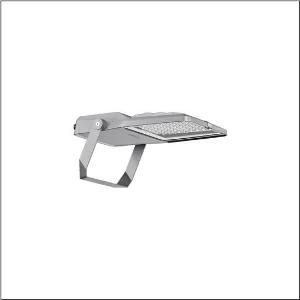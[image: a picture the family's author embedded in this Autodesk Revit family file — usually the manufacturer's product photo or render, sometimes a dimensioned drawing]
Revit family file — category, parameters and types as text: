
# Revit family: floodlight_fl_21_iq_mini___rs12_5xa7772b1b1a_07b1
name_source: partatom
category: Lighting Fixtures
units: mm (PartAtom-declared; Revit-internal decimal feet)

## family parameters
Cut with Voids When Loaded = No
Host = Face
Light Source = No
Part Type = Normal
Room Calculation Point = No
Round Connector Dimension = Use Diameter
Shared = No

## types (1)
- --- (1 x LED, 5230 lm, 45.5 W, 2200K)
    Apparent Load = 46 VA
    CIE Flux Codes = 79 92 99 100 100
    Color Rendering = 70
    Color Temperature = 2200K
    Default Elevation = 1800 mm
    Description = Floodlight FL 21 iQ mini, floodlight, primary light control with lens, of PMMA, primary optical cover: protective disc, of toughened safety glass, transparent, light distribution: RS12, light emission: direct distribution, installation type: surface-mounted, LED, High Power LED, rated luminous flux: 5.230lm, luminous efficacy: 115lm/W, light colour: 722, colour temperature: 2200K, control: Street-Remote, Auto-Match, Temp-Guard, Night-Set, Smart-Wire, Desk-Remote (wireless, voltage-free reading and setting of iQ features in the workshop via application-optimized NFC function/RFID function), optimised constant luminous flux control (CLO 2.0), with terminal, 6-pole, mains connection: 220..240V, AC, 50/60Hz, start of lifetime: 46W, end of service life: 48W, reduction: 21W, luminaire housing, of diecast aluminium, powder-coated, Siteco® metallic grey (DB 702S), corrosivity category C5 mid according to DIN EN ISO 12944, sealing non-destructively replaceable, mounting bracket, of steel, galvanised, powder-coated, Siteco® metallic grey (DB 702S), protection rating (complete): IP66, insulation class (complete): insulation class II (safety insulation), certification: CE, ENEC, VDE, protection symbol: D, impact resistance: IK08, permissible operating ambient temperature: -40..+40°C, permissible operating ambient temperature for outdoor applications: -40..+50°C, standard: DIN EN 12944, LABS conformity tested according to VDMA 24364:2018-05, packaging unit: 1 piece

Light Distribution: RS12
    Height = 70 mm
    Lamp = 1 x LED
    Lamp Light Flux = 5230 lm
    Lamp Power = 45.5 W
    Lamp count = 1
    Length = 485 mm
    Luminous efficacy = 115 lm/W
    Manufacturer = Siteco
    ModVariant = No
    Model = 5XA7772B1B1A
    Number of Poles = 1
    OnlyDefault = Yes
    Power Factor = 1
    Product Name = Floodlight FL 21 iQ mini | RS12
    Product group = floodlight | pylon annexe
    ProductGroupID = 6200
    Protection Class = Protection class II
    Protection Degree = IP 66
    RLX_Detail_Level = 1
    RLX_Emergency_Light_Flux = 0 lm
    RLX_Emergency_Type = 0
    RLX_Emergency_Type_DB = No
    RlxData = <blob elided: 90849 chars, md5=d1231205>
    Socket = socket
    Standby Power = 0 W
    System Light Flux = 5230 lm
    System Power = 46 W
    Type Comments = factory setting: luminous flux: 100 % | dim-lin: 254 | 463 mA
    Type Image = l_1006845.jpg
    URL = http://relux.com
    VarID = @adj_118091
    Voltage = 0 V
    Weight = 0.00 kg
    Width = 337 mm

## geometry (parser evidence)
native form markers: Blend x4, Sweep x14
no freeform markers — native parametric forms only
